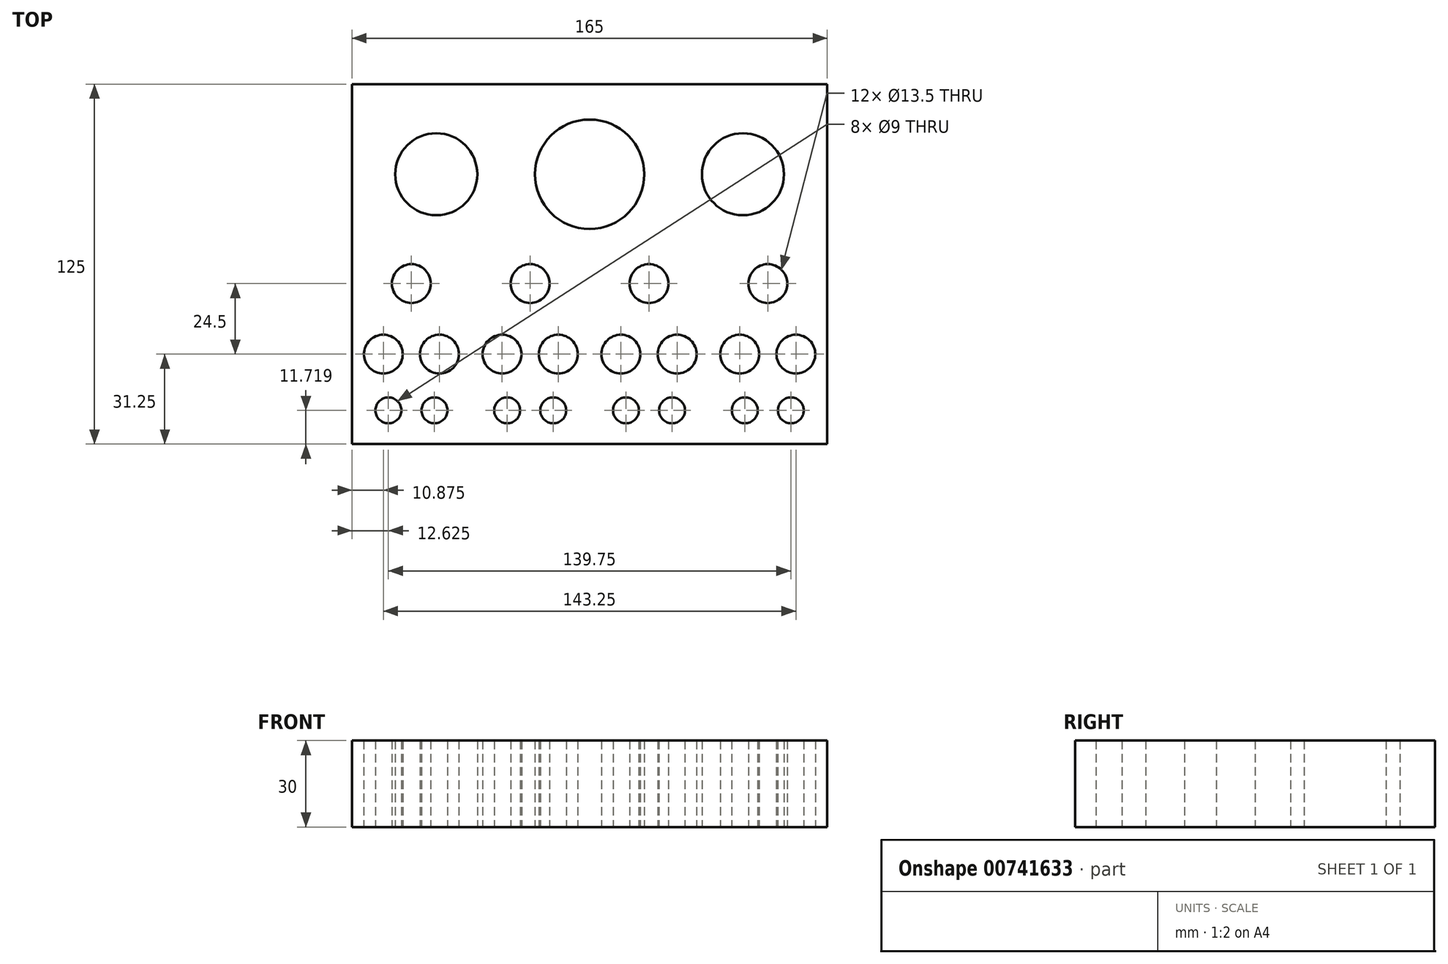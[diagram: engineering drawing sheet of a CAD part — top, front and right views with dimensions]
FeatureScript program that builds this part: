
annotation { "Feature Type Name" : "Feature", "Feature Type Description" : "" }
export const myFeature = defineFeature(function(context is Context, id is Id, definition is map)
    precondition{}
    {
        {
            var Q0;
            Q0=qCreatedBy(makeId("Top.planeOp"),FACE);
            var sketch = newSketch(context, id + "F0", { "sketchPlane" : qUnion([Q0])});
            skLineSegment(sketch, "E0.bottom", {"start": v(-165, 125) * mm, "end": v(0, 125) * mm});
            skLineSegment(sketch, "E0.top", {"start": v(-165, 0) * mm, "end": v(0, 0) * mm});
            skLineSegment(sketch, "E0.left", {"start": v(-165, 125) * mm, "end": v(-165, 0) * mm});
            skLineSegment(sketch, "E0.right", {"start": v(0, 125) * mm, "end": v(0, 0) * mm});
            skLineSegment(sketch, "E1", {"start": v(-82.5, 125) * mm, "end": v(-82.5, 0) * mm, "construction": true});
            skLineSegment(sketch, "E2", {"start": v(-165, 62.5) * mm, "end": v(0, 62.5) * mm, "construction": true});
            skLineSegment(sketch, "E3", {"start": v(-165, 62.5) * mm, "end": v(-165, 125) * mm, "construction": true});
            skLineSegment(sketch, "E4", {"start": v(-165, 93.75) * mm, "end": v(0, 93.75) * mm, "construction": true});
            skLineSegment(sketch, "E5", {"start": v(-82.5, 125) * mm, "end": v(-165, 125) * mm, "construction": true});
            skLineSegment(sketch, "E6", {"start": v(-123.75, 125) * mm, "end": v(-123.75, 0) * mm, "construction": true});
            skLineSegment(sketch, "E7", {"start": v(-165, 62.5) * mm, "end": v(-165, 0) * mm, "construction": true});
            skLineSegment(sketch, "E8", {"start": v(-165, 31.25) * mm, "end": v(0, 31.25) * mm, "construction": true});
            skLineSegment(sketch, "E9", {"start": v(-123.75, 125) * mm, "end": v(-82.5, 125) * mm, "construction": true});
            skLineSegment(sketch, "E10", {"start": v(-103.12, 125) * mm, "end": v(-103.12, 0) * mm, "construction": true});
            skLineSegment(sketch, "E11", {"start": v(-165, 93.75) * mm, "end": v(-150, 93.75) * mm, "construction": true});
            skCircle(sketch, "E12", {"center": v(-135.75, 93.75) * mm, "radius": 14.25 * mm});
            skCircle(sketch, "E13", {"center": v(-103.13, 55.75) * mm, "radius": 6.75 * mm});
            skLineSegment(sketch, "E14", {"start": v(-123.75, 31.25) * mm, "end": v(-103.13, 31.25) * mm, "construction": true});
            skCircle(sketch, "E15", {"center": v(-112.88, 31.25) * mm, "radius": 6.75 * mm});
            skCircle(sketch, "E16.MirrorC", {"center": v(-93.38, 31.25) * mm, "radius": 6.75 * mm});
            skLineSegment(sketch, "E17", {"start": v(-103.12, 31.25) * mm, "end": v(-103.12, 0) * mm, "construction": true});
            skLineSegment(sketch, "E18", {"start": v(-103.13, 15.62) * mm, "end": v(-82.5, 15.63) * mm, "construction": true});
            skLineSegment(sketch, "E19", {"start": v(-103.12, 15.62) * mm, "end": v(-103.12, 0) * mm, "construction": true});
            skCircle(sketch, "E20", {"center": v(-95.12, 11.72) * mm, "radius": 4.5 * mm});
            skCircle(sketch, "E21.MirrorC", {"center": v(-111.13, 11.72) * mm, "radius": 4.5 * mm});
            skCircle(sketch, "E22.MirrorC", {"center": v(-152.38, 11.72) * mm, "radius": 4.5 * mm});
            skCircle(sketch, "E23.MirrorC", {"center": v(-136.38, 11.72) * mm, "radius": 4.5 * mm});
            skCircle(sketch, "E24.MirrorC", {"center": v(-144.38, 55.75) * mm, "radius": 6.75 * mm});
            skCircle(sketch, "E25.MirrorC", {"center": v(-134.63, 31.25) * mm, "radius": 6.75 * mm});
            skCircle(sketch, "E26.MirrorC", {"center": v(-154.13, 31.25) * mm, "radius": 6.75 * mm});
            skCircle(sketch, "E27.MirrorC", {"center": v(-29.25, 93.75) * mm, "radius": 14.25 * mm});
            skCircle(sketch, "E28.MirrorC", {"center": v(-20.63, 55.75) * mm, "radius": 6.75 * mm});
            skCircle(sketch, "E29.MirrorC", {"center": v(-30.38, 31.25) * mm, "radius": 6.75 * mm});
            skCircle(sketch, "E30.MirrorC", {"center": v(-10.87, 31.25) * mm, "radius": 6.75 * mm});
            skCircle(sketch, "E31.MirrorC", {"center": v(-12.62, 11.72) * mm, "radius": 4.5 * mm});
            skCircle(sketch, "E32.MirrorC", {"center": v(-28.63, 11.72) * mm, "radius": 4.5 * mm});
            skCircle(sketch, "E33.MirrorC", {"center": v(-69.88, 11.72) * mm, "radius": 4.5 * mm});
            skCircle(sketch, "E34.MirrorC", {"center": v(-53.88, 11.72) * mm, "radius": 4.5 * mm});
            skCircle(sketch, "E35.MirrorC", {"center": v(-52.13, 31.25) * mm, "radius": 6.75 * mm});
            skCircle(sketch, "E36.MirrorC", {"center": v(-71.63, 31.25) * mm, "radius": 6.75 * mm});
            skCircle(sketch, "E37.MirrorC", {"center": v(-61.88, 55.75) * mm, "radius": 6.75 * mm});
            skCircle(sketch, "E38", {"center": v(-82.5, 93.75) * mm, "radius": 19 * mm});
            skLineSegment(sketch, "E39", {"start": v(-160.88, 31.25) * mm, "end": v(-165, 31.25) * mm, "construction": true});
            skLineSegment(sketch, "E40", {"start": v(-103.13, 15.62) * mm, "end": v(-103.13, 7.81) * mm, "construction": true});
            skLineSegment(sketch, "E41", {"start": v(-103.13, 11.72) * mm, "end": v(-82.5, 11.72) * mm, "construction": true});
            skLineSegment(sketch, "E42", {"start": v(-103.13, 11.72) * mm, "end": v(-99.62, 11.72) * mm, "construction": true});
            skLineSegment(sketch, "E43", {"start": v(-103.13, 31.25) * mm, "end": v(-106.13, 31.25) * mm, "construction": true});
            skSolve(sketch);
        }
        {
            var Q0;
            Q0=makeQuery(id+"F0.imprint","IMPRINT",FACE,{"disambiguationData":[TD([[makeQuery(id+"F0.imprint","IMPRINT",EDGE,{"derivedFrom":sQuery(id+"F0.wireOp",EDGE,"E0.bottom")}),-1.0]])]});
            extrude(context, id + "F1", {"entities" : qUnion([Q0]), "depth" : 30 * mm, "offsetDistance" : 25 * mm});
        }
    });
